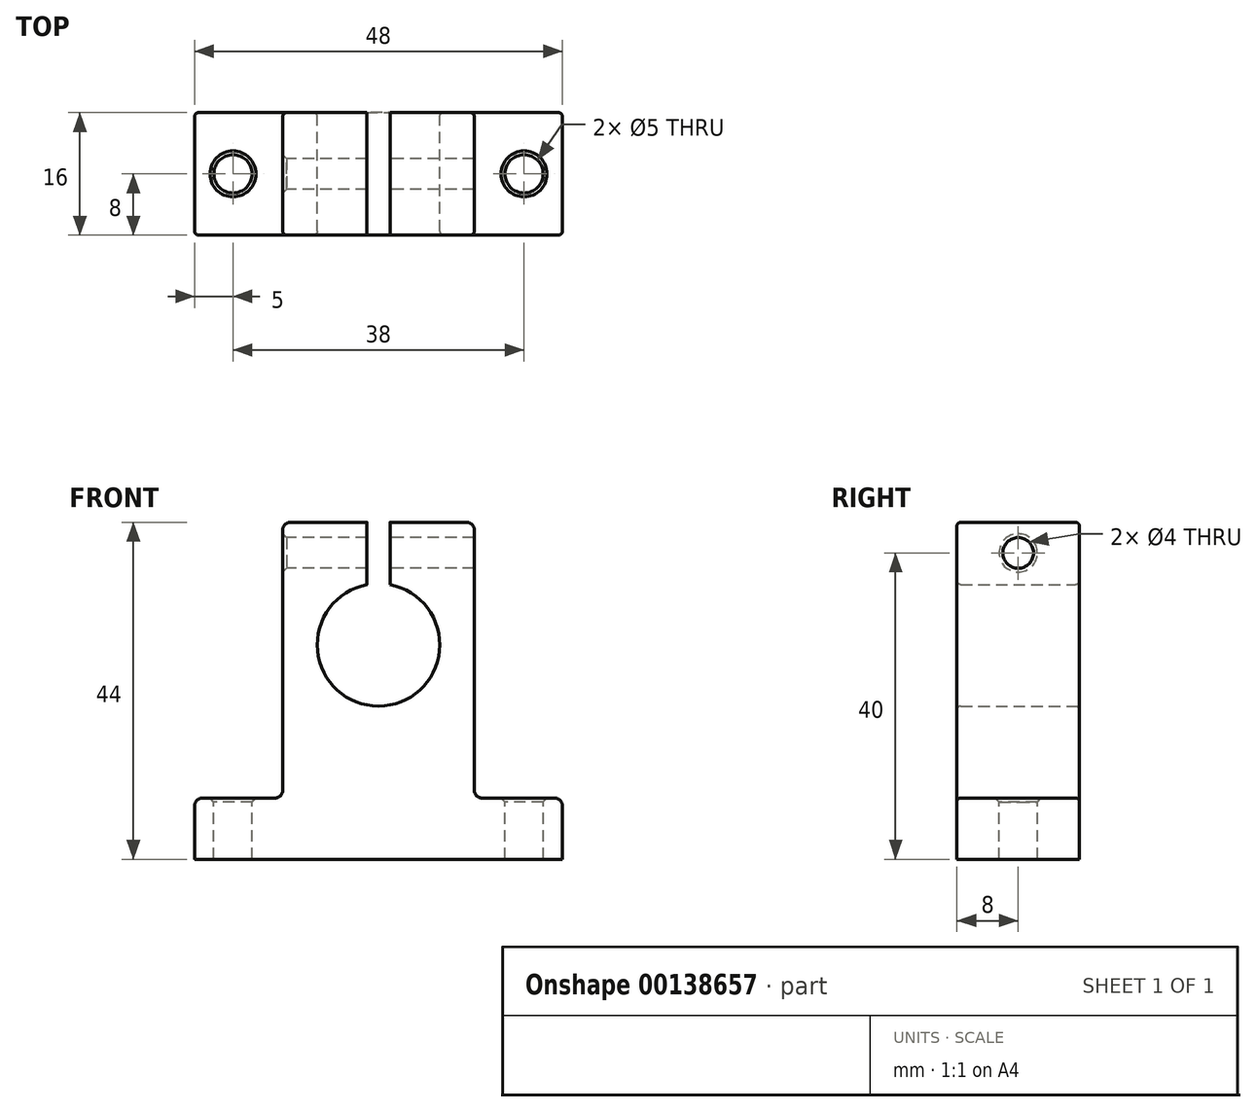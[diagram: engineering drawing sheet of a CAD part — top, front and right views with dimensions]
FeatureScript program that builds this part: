
annotation { "Feature Type Name" : "Feature", "Feature Type Description" : "" }
export const myFeature = defineFeature(function(context is Context, id is Id, definition is map)
    precondition{}
    {
        {
            var Q0;
            Q0=qCreatedBy(makeId("Front.planeOp"),FACE);
            var sketch = newSketch(context, id + "F0", { "sketchPlane" : qUnion([Q0])});
            skLineSegment(sketch, "E0", {"start": v(24, 0) * mm, "end": v(-24, 0) * mm});
            skLineSegment(sketch, "E1", {"start": v(-24, 0) * mm, "end": v(-24, 7) * mm});
            skLineSegment(sketch, "E2", {"start": v(-23, 8) * mm, "end": v(-13.5, 8) * mm});
            skLineSegment(sketch, "E3", {"start": v(-12.5, 9) * mm, "end": v(-12.5, 43) * mm});
            skLineSegment(sketch, "E4", {"start": v(-11.5, 44) * mm, "end": v(-1.5, 44) * mm});
            skLineSegment(sketch, "E5", {"start": v(12.5, 43) * mm, "end": v(12.5, 9) * mm});
            skLineSegment(sketch, "E6", {"start": v(13.5, 8) * mm, "end": v(23, 8) * mm});
            skLineSegment(sketch, "E7", {"start": v(24, 7) * mm, "end": v(24, 0) * mm});
            skLineSegment(sketch, "E8", {"start": v(0, 0) * mm, "end": v(0, 36.7) * mm, "construction": true});
            skArc(sketch, "E9", {"start": v(-1.5, 35.86) * mm, "mid": v(0, 20) * mm, "end": v(1.5, 35.86) * mm});
            skPoint(sketch, "E10.visualSharp", {"position": v(-12.5, 44) * mm});
            skArc(sketch, "E10.filletArc", {"start": v(-11.5, 44) * mm, "mid": v(-12.2, 43.7) * mm, "end": v(-12.5, 43) * mm});
            skPoint(sketch, "E11.visualSharp", {"position": v(12.5, 44) * mm});
            skArc(sketch, "E11.filletArc", {"start": v(12.5, 43) * mm, "mid": v(12.2, 43.7) * mm, "end": v(11.5, 44) * mm});
            skPoint(sketch, "E12.visualSharp", {"position": v(-12.5, 8) * mm});
            skArc(sketch, "E12.filletArc", {"start": v(-13.5, 8) * mm, "mid": v(-12.8, 8.3) * mm, "end": v(-12.5, 9) * mm});
            skPoint(sketch, "E13.visualSharp", {"position": v(12.5, 8) * mm});
            skArc(sketch, "E13.filletArc", {"start": v(12.5, 9) * mm, "mid": v(12.8, 8.3) * mm, "end": v(13.5, 8) * mm});
            skPoint(sketch, "E14.visualSharp", {"position": v(-24, 8) * mm});
            skArc(sketch, "E14.filletArc", {"start": v(-23, 8) * mm, "mid": v(-23.7, 7.7) * mm, "end": v(-24, 7) * mm});
            skPoint(sketch, "E15.visualSharp", {"position": v(24, 8) * mm});
            skArc(sketch, "E15.filletArc", {"start": v(24, 7) * mm, "mid": v(23.7, 7.7) * mm, "end": v(23, 8) * mm});
            skLineSegment(sketch, "E16", {"start": v(-1.5, 44) * mm, "end": v(-1.5, 35.86) * mm});
            skLineSegment(sketch, "E17.MirrorCS", {"start": v(1.5, 44) * mm, "end": v(1.5, 35.86) * mm});
            skLineSegment(sketch, "E18.trimOffspring", {"start": v(1.5, 44) * mm, "end": v(11.5, 44) * mm});
            skPoint(sketch, "E19.orphan", {"position": v(-1.5, 47.5) * mm});
            skPoint(sketch, "E20.orphan", {"position": v(1.5, 47.5) * mm});
            skSolve(sketch);
        }
        {
            var Q0;
            Q0 = qSketchRegion(id + "F0", true);
            extrude(context, id + "F1", {"entities" : qUnion([Q0]), "endBound" : BoundingType.SYMMETRIC, "depth" : 16 * mm});
        }
        {
            var Q0;
            Q0=makeQuery(id+"F1.opExtrude","SWEPT_FACE",FACE,{"disambiguationData":[OSD([sQuery(id+"F0.wireOp",EDGE,"E6")])]});
            var sketch = newSketch(context, id + "F2", { "sketchPlane" : qUnion([Q0])});
            skPoint(sketch, "E21", {"position": v(19, 0) * mm});
            skPoint(sketch, "E22.MirrorP", {"position": v(-19, 0) * mm});
            skSolve(sketch);
        }
        {
            var Q0;
            Q0=sQuery(id+"F2.wireOp",VERTEX,"E22.MirrorP");
            var Q1;
            Q1=sQuery(id+"F2.wireOp",VERTEX,"E21");
            var Q2;
            Q2=makeQuery(id+"F1.opExtrude","SWEPT_BODY",BODY,{"disambiguationData":[OSD([sQuery(id+"F0.wireOp",EDGE,"E0"),sQuery(id+"F0.wireOp",EDGE,"E1"),sQuery(id+"F0.wireOp",EDGE,"E2"),sQuery(id+"F0.wireOp",EDGE,"E3"),sQuery(id+"F0.wireOp",EDGE,"E4"),sQuery(id+"F0.wireOp",EDGE,"E5"),sQuery(id+"F0.wireOp",EDGE,"E6"),sQuery(id+"F0.wireOp",EDGE,"E7"),sQuery(id+"F0.wireOp",EDGE,"E9"),sQuery(id+"F0.wireOp",EDGE,"E10.filletArc"),sQuery(id+"F0.wireOp",EDGE,"E11.filletArc"),sQuery(id+"F0.wireOp",EDGE,"E12.filletArc"),sQuery(id+"F0.wireOp",EDGE,"E13.filletArc"),sQuery(id+"F0.wireOp",EDGE,"E14.filletArc"),sQuery(id+"F0.wireOp",EDGE,"E15.filletArc"),sQuery(id+"F0.wireOp",EDGE,"E16"),sQuery(id+"F0.wireOp",EDGE,"E17.MirrorCS"),sQuery(id+"F0.wireOp",EDGE,"E18.trimOffspring")])]});
            hole(context, id + "F3", {"style" : HoleStyle.C_SINK, "endStyle" : HoleEndStyle.THROUGH, "holeDiameter" : 5 * mm, "cSinkDiameter" : 6 * mm, "cSinkAngle" : 90 * degree, "locations" : qUnion([Q0, Q1]), "scope" : qUnion([Q2]), "isTappedThrough" : true});
        }
        {
            var Q0;
            Q0=makeQuery(id+"F1.opExtrude","CAP_EDGE",EDGE,{"disambiguationData":[OSD([sQuery(id+"F0.wireOp",EDGE,"E5")])],"isStart":false});
            var Q1;
            Q1=makeQuery(id+"F1.opExtrude","CAP_EDGE",EDGE,{"disambiguationData":[OSD([sQuery(id+"F0.wireOp",EDGE,"E3")])],"isStart":false});
            var Q2;
            Q2=makeQuery(id+"F1.opExtrude","CAP_EDGE",EDGE,{"disambiguationData":[OSD([sQuery(id+"F0.wireOp",EDGE,"E3")])],"isStart":true});
            var Q3;
            Q3=makeQuery(id+"F1.opExtrude","CAP_EDGE",EDGE,{"disambiguationData":[OSD([sQuery(id+"F0.wireOp",EDGE,"E5")])],"isStart":true});
            var Q4;
            Q4=makeQuery(id+"F1.opExtrude","CAP_EDGE",EDGE,{"disambiguationData":[OSD([sQuery(id+"F0.wireOp",EDGE,"E9")])],"isStart":false});
            var Q5;
            Q5=makeQuery(id+"F1.opExtrude","CAP_EDGE",EDGE,{"disambiguationData":[OSD([sQuery(id+"F0.wireOp",EDGE,"E9")])],"isStart":true});
            fillet(context, id + "F4", {"entities" : qUnion([Q0, Q1, Q2, Q3, Q4, Q5]), "radius" : 0.5 * mm, "tangentPropagation" : true, "allowEdgeOverflow" : false});
        }
        {
            var Q0;
            Q0=makeQuery(id+"F1.opExtrude","SWEPT_FACE",FACE,{"disambiguationData":[OSD([sQuery(id+"F0.wireOp",EDGE,"E3")])]});
            var sketch = newSketch(context, id + "F5", { "sketchPlane" : qUnion([Q0])});
            skCircle(sketch, "E23", {"center": v(0, 40) * mm, "radius": 2 * mm});
            skPoint(sketch, "E23.centerSnap0", {"position": v(0, 43) * mm});
            skSolve(sketch);
        }
        {
            var Q0;
            Q0=sQuery(id+"F5.wireOp",VERTEX,"E23.center");
            var Q1;
            Q1=makeQuery(id+"F1.opExtrude","SWEPT_BODY",BODY,{"disambiguationData":[OSD([sQuery(id+"F0.wireOp",EDGE,"E0"),sQuery(id+"F0.wireOp",EDGE,"E1"),sQuery(id+"F0.wireOp",EDGE,"E2"),sQuery(id+"F0.wireOp",EDGE,"E3"),sQuery(id+"F0.wireOp",EDGE,"E4"),sQuery(id+"F0.wireOp",EDGE,"E5"),sQuery(id+"F0.wireOp",EDGE,"E6"),sQuery(id+"F0.wireOp",EDGE,"E7"),sQuery(id+"F0.wireOp",EDGE,"E9"),sQuery(id+"F0.wireOp",EDGE,"E10.filletArc"),sQuery(id+"F0.wireOp",EDGE,"E11.filletArc"),sQuery(id+"F0.wireOp",EDGE,"E12.filletArc"),sQuery(id+"F0.wireOp",EDGE,"E13.filletArc"),sQuery(id+"F0.wireOp",EDGE,"E14.filletArc"),sQuery(id+"F0.wireOp",EDGE,"E15.filletArc"),sQuery(id+"F0.wireOp",EDGE,"E16"),sQuery(id+"F0.wireOp",EDGE,"E17.MirrorCS"),sQuery(id+"F0.wireOp",EDGE,"E18.trimOffspring")])]});
            hole(context, id + "F6", {"style" : HoleStyle.C_SINK, "endStyle" : HoleEndStyle.THROUGH, "holeDiameter" : 4 * mm, "cSinkDiameter" : 5 * mm, "cSinkAngle" : 90 * degree, "locations" : qUnion([Q0]), "scope" : qUnion([Q1]), "isTappedThrough" : true});
        }
    });
